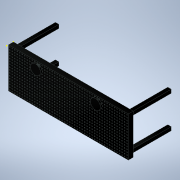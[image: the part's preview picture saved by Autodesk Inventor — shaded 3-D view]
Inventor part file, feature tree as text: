
AUTODESK INVENTOR PART (.ipt)
format: ipt  version: 2020 (Build 240168000, 168)  size: 1,390,080 bytes
history: native  units: mm
features: extrude x8, sketch x7
ambient origin geometry x8: Origin, YZ Plane, XZ Plane, XY Plane, X Axis, Y Axis, Z Axis, Center Point
bodies: Solid1 (feature_tree)
feature tree (15):
  sketch  "Sketch1"  dims[d0=2400.0mm d1=800.0mm]
  extrude  "Extrusion1"  Depth=800.0mm
  extrude  "Extrusion2"  Depth=125.0mm
  sketch  "Sketch2"  dims[d2=575.0mm d3=125.0mm]
  extrude  "Extrusion3"  Depth=1775.0mm
  extrude  "Extrusion4"  Depth=100.0mm TaperAngle=0.0deg
  sketch  "Sketch3"  dims[d4=1775.0mm d5=200.0mm]
  extrude  "Extrusion5"  Depth=100.0mm TaperAngle=0.0deg
  extrude  "Extrusion6"  Depth=40.0mm
  extrude  "Extrusion7"  Depth=70.0mm
  extrude  "Extrusion8"  Depth=40.0mm
  sketch  "Sketch4"  dims[d6=35.0mm d7=0.0mm d8=100.0mm d9=0.0mm]
  sketch  "Sketch5"  dims[d10=100.0mm d11=0.0mm d12=100.0mm d13=0.0mm]
  sketch  "Sketch6"  dims[d14=40.0mm d15=40.0mm]
  sketch  "Sketch7"  dims[d16=70.0mm d17=70.0mm d18=40.0mm d19=40.0mm d20=70.0mm d21=70.0mm d22=40.0mm d23=40.0mm d24=70.0mm d25=70.0mm d26=70.0mm d27=70.0mm d28=800.0mm d29=0.0mm d34=135.25mm d35=0.0mm d36=70.0mm d37=0.0mm d38=70.0mm d39=0.0mm]
